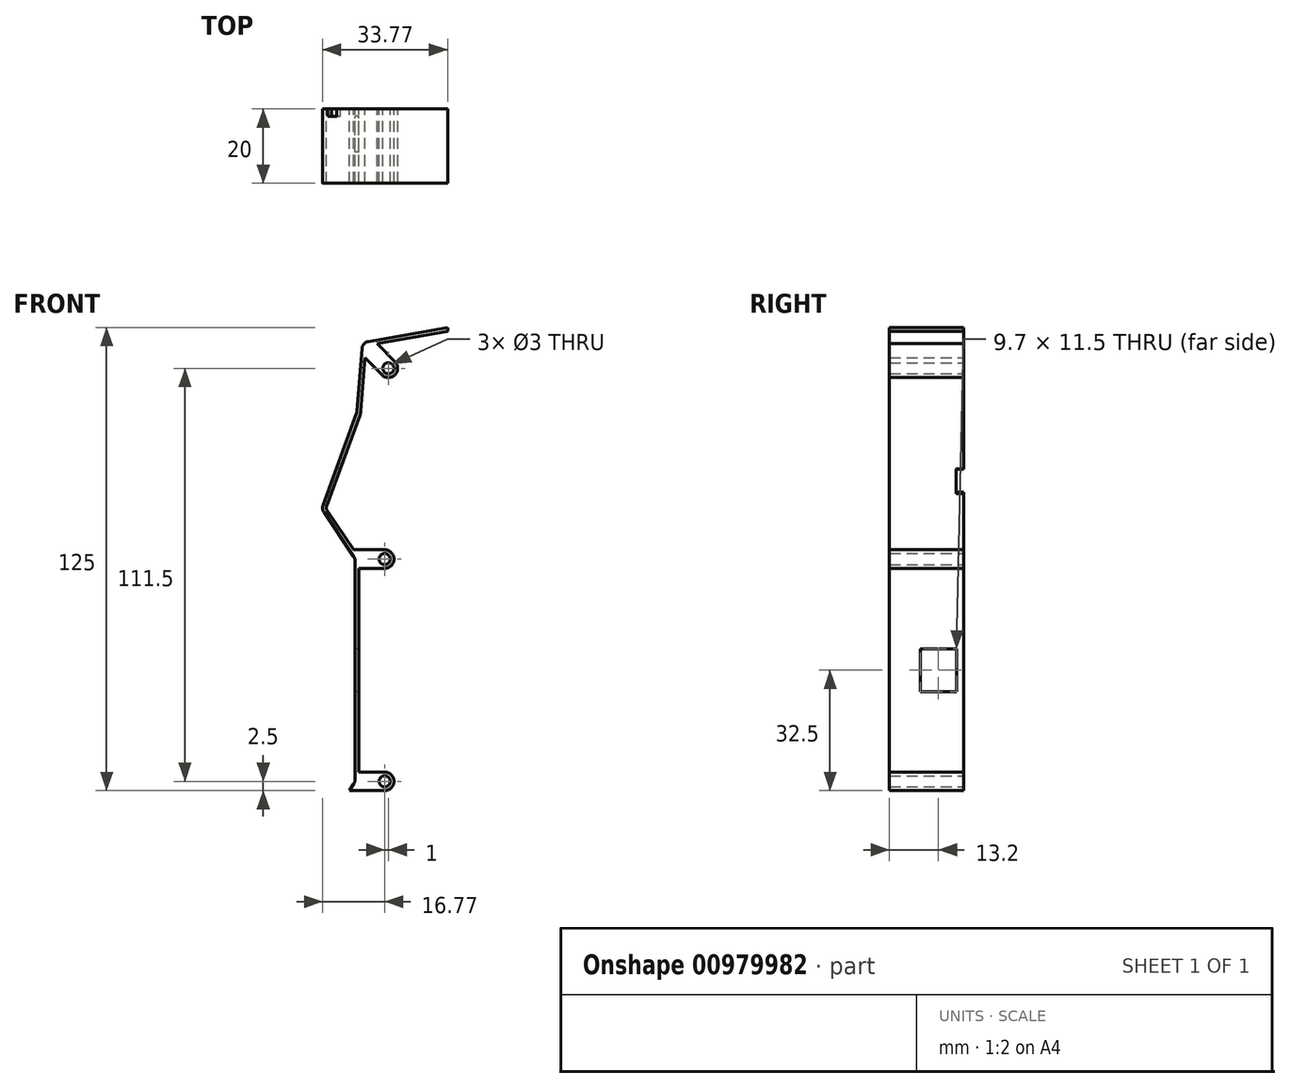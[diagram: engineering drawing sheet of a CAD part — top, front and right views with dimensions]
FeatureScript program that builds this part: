
annotation { "Feature Type Name" : "Feature", "Feature Type Description" : "" }
export const myFeature = defineFeature(function(context is Context, id is Id, definition is map)
    precondition{}
    {
        {
            var Q0;
            Q0=qCreatedBy(makeId("Front.planeOp"),FACE);
            var sketch = newSketch(context, id + "F0", { "sketchPlane" : qUnion([Q0])});
            skLineSegment(sketch, "E0", {"start": v(13, -77) * mm, "end": v(6, -77) * mm});
            skArc(sketch, "E1", {"start": v(33.65, -43.96) * mm, "mid": v(33.76, -43.03) * mm, "end": v(33.43, -42.16) * mm});
            skArc(sketch, "E2", {"start": v(33.43, 42.16) * mm, "mid": v(33.76, 43.03) * mm, "end": v(33.65, 43.96) * mm});
            skArc(sketch, "E3", {"start": v(-33.65, 43.96) * mm, "mid": v(-33.76, 43.03) * mm, "end": v(-33.43, 42.16) * mm});
            skArc(sketch, "E4", {"start": v(-33.43, -42.16) * mm, "mid": v(-33.76, -43.03) * mm, "end": v(-33.65, -43.96) * mm});
            skCircle(sketch, "E5", {"center": v(16, 81) * mm, "radius": 1.5 * mm});
            skCircle(sketch, "E6", {"center": v(0, 76) * mm, "radius": 1.5 * mm});
            skCircle(sketch, "E7", {"center": v(26.67, 45.42) * mm, "radius": 1.5 * mm});
            skCircle(sketch, "E8", {"center": v(22.4, 57.17) * mm, "radius": 1.5 * mm});
            skCircle(sketch, "E9", {"center": v(17.28, 42) * mm, "radius": 1.5 * mm});
            skCircle(sketch, "E10", {"center": v(13, 53.75) * mm, "radius": 1.5 * mm});
            skCircle(sketch, "E11", {"center": v(17, 29.5) * mm, "radius": 1.5 * mm});
            skCircle(sketch, "E12", {"center": v(15.25, 15.25) * mm, "radius": 1.5 * mm});
            skCircle(sketch, "E13", {"center": v(-15.25, 15.25) * mm, "radius": 1.5 * mm});
            skCircle(sketch, "E14", {"center": v(-17, 29.5) * mm, "radius": 1.5 * mm});
            skCircle(sketch, "E15", {"center": v(-13, 53.75) * mm, "radius": 1.5 * mm});
            skCircle(sketch, "E16", {"center": v(-17.28, 42) * mm, "radius": 1.5 * mm});
            skCircle(sketch, "E17", {"center": v(-22.4, 57.17) * mm, "radius": 1.5 * mm});
            skCircle(sketch, "E18", {"center": v(-26.67, 45.42) * mm, "radius": 1.5 * mm});
            skCircle(sketch, "E19", {"center": v(-16, 81) * mm, "radius": 1.5 * mm});
            skCircle(sketch, "E20", {"center": v(-16, -81) * mm, "radius": 1.5 * mm});
            skCircle(sketch, "E21", {"center": v(-26.67, -45.42) * mm, "radius": 1.5 * mm});
            skCircle(sketch, "E22", {"center": v(-22.4, -57.17) * mm, "radius": 1.5 * mm});
            skCircle(sketch, "E23", {"center": v(-17.28, -42) * mm, "radius": 1.5 * mm});
            skCircle(sketch, "E24", {"center": v(-13, -53.75) * mm, "radius": 1.5 * mm});
            skCircle(sketch, "E25", {"center": v(-17, -29.5) * mm, "radius": 1.5 * mm});
            skCircle(sketch, "E26", {"center": v(-15.25, -15.25) * mm, "radius": 1.5 * mm});
            skCircle(sketch, "E27", {"center": v(15.25, -15.25) * mm, "radius": 1.5 * mm});
            skCircle(sketch, "E28", {"center": v(17, -29.5) * mm, "radius": 1.5 * mm});
            skCircle(sketch, "E29", {"center": v(13, -53.75) * mm, "radius": 1.5 * mm});
            skCircle(sketch, "E30", {"center": v(17.28, -42) * mm, "radius": 1.5 * mm});
            skCircle(sketch, "E31", {"center": v(22.4, -57.17) * mm, "radius": 1.5 * mm});
            skCircle(sketch, "E32", {"center": v(26.67, -45.42) * mm, "radius": 1.5 * mm});
            skCircle(sketch, "E33", {"center": v(0, -76) * mm, "radius": 1.5 * mm});
            skCircle(sketch, "E34", {"center": v(16, -81) * mm, "radius": 1.5 * mm});
            skLineSegment(sketch, "E35", {"start": v(25.34, 30.16) * mm, "end": v(33.43, 42.16) * mm});
            skLineSegment(sketch, "E36", {"start": v(33.65, 43.96) * mm, "end": v(24.57, 68.9) * mm});
            skArc(sketch, "E37", {"start": v(24.46, 69.43) * mm, "mid": v(24.5, 69.16) * mm, "end": v(24.57, 68.9) * mm});
            skLineSegment(sketch, "E38", {"start": v(24.46, 69.43) * mm, "end": v(23.12, 86.4) * mm});
            skArc(sketch, "E39", {"start": v(23.12, 86.4) * mm, "mid": v(22.6, 87.59) * mm, "end": v(21.47, 88.21) * mm});
            skLineSegment(sketch, "E40", {"start": v(21.47, 88.21) * mm, "end": v(0, 92) * mm});
            skLineSegment(sketch, "E41", {"start": v(0, 92) * mm, "end": v(-21.47, 88.21) * mm});
            skArc(sketch, "E42", {"start": v(-21.47, 88.21) * mm, "mid": v(-22.6, 87.59) * mm, "end": v(-23.12, 86.4) * mm});
            skLineSegment(sketch, "E43", {"start": v(-23.12, 86.4) * mm, "end": v(-24.46, 69.43) * mm});
            skArc(sketch, "E44", {"start": v(-24.57, 68.9) * mm, "mid": v(-24.5, 69.16) * mm, "end": v(-24.46, 69.43) * mm});
            skLineSegment(sketch, "E45", {"start": v(-24.57, 68.9) * mm, "end": v(-33.65, 43.96) * mm});
            skLineSegment(sketch, "E46", {"start": v(-33.43, 42.16) * mm, "end": v(-25.34, 30.16) * mm});
            skArc(sketch, "E47", {"start": v(-25, 29.05) * mm, "mid": v(-25.09, 29.63) * mm, "end": v(-25.34, 30.16) * mm});
            skLineSegment(sketch, "E48", {"start": v(-25, 29.05) * mm, "end": v(-25, -29.05) * mm});
            skArc(sketch, "E49", {"start": v(-25.34, -30.16) * mm, "mid": v(-25.09, -29.63) * mm, "end": v(-25, -29.05) * mm});
            skLineSegment(sketch, "E50", {"start": v(-25.34, -30.16) * mm, "end": v(-33.43, -42.16) * mm});
            skLineSegment(sketch, "E51", {"start": v(-33.65, -43.96) * mm, "end": v(-24.57, -68.9) * mm});
            skArc(sketch, "E52", {"start": v(-24.46, -69.43) * mm, "mid": v(-24.5, -69.16) * mm, "end": v(-24.57, -68.9) * mm});
            skLineSegment(sketch, "E53", {"start": v(-24.46, -69.43) * mm, "end": v(-23.12, -86.4) * mm});
            skArc(sketch, "E54", {"start": v(-23.12, -86.4) * mm, "mid": v(-22.6, -87.59) * mm, "end": v(-21.47, -88.21) * mm});
            skLineSegment(sketch, "E55", {"start": v(-21.47, -88.21) * mm, "end": v(0, -92) * mm});
            skLineSegment(sketch, "E56", {"start": v(0, -92) * mm, "end": v(21.47, -88.21) * mm});
            skArc(sketch, "E57", {"start": v(21.47, -88.21) * mm, "mid": v(22.6, -87.59) * mm, "end": v(23.12, -86.4) * mm});
            skLineSegment(sketch, "E58", {"start": v(23.12, -86.4) * mm, "end": v(24.46, -69.43) * mm});
            skArc(sketch, "E59", {"start": v(24.57, -68.9) * mm, "mid": v(24.5, -69.16) * mm, "end": v(24.46, -69.43) * mm});
            skLineSegment(sketch, "E60", {"start": v(24.57, -68.9) * mm, "end": v(33.65, -43.96) * mm});
            skLineSegment(sketch, "E61", {"start": v(33.43, -42.16) * mm, "end": v(25.34, -30.16) * mm});
            skArc(sketch, "E62", {"start": v(25, -29.05) * mm, "mid": v(25.09, -29.63) * mm, "end": v(25.34, -30.16) * mm});
            skLineSegment(sketch, "E63", {"start": v(25, -29.05) * mm, "end": v(25, 29.05) * mm});
            skArc(sketch, "E64", {"start": v(25.34, 30.16) * mm, "mid": v(25.09, 29.63) * mm, "end": v(25, 29.05) * mm});
            skArc(sketch, "E65", {"start": v(14.5, -75) * mm, "mid": v(13.75, -74.25) * mm, "end": v(13, -75) * mm});
            skLineSegment(sketch, "E66", {"start": v(14.5, -75) * mm, "end": v(14.5, -77) * mm});
            skArc(sketch, "E67", {"start": v(13, -77) * mm, "mid": v(13.75, -77.75) * mm, "end": v(14.5, -77) * mm});
            skArc(sketch, "E68", {"start": v(4.5, -77) * mm, "mid": v(5.25, -77.75) * mm, "end": v(6, -77) * mm});
            skLineSegment(sketch, "E69", {"start": v(4.5, -77) * mm, "end": v(4.5, -75) * mm});
            skArc(sketch, "E70", {"start": v(6, -75) * mm, "mid": v(5.25, -74.25) * mm, "end": v(4.5, -75) * mm});
            skLineSegment(sketch, "E71", {"start": v(6, -75) * mm, "end": v(13, -75) * mm});
            skArc(sketch, "E72", {"start": v(-4.5, -75) * mm, "mid": v(-5.25, -74.25) * mm, "end": v(-6, -75) * mm});
            skLineSegment(sketch, "E73", {"start": v(-4.5, -75) * mm, "end": v(-4.5, -77) * mm});
            skArc(sketch, "E74", {"start": v(-6, -77) * mm, "mid": v(-5.25, -77.75) * mm, "end": v(-4.5, -77) * mm});
            skLineSegment(sketch, "E75", {"start": v(-6, -77) * mm, "end": v(-13, -77) * mm});
            skArc(sketch, "E76", {"start": v(-14.5, -77) * mm, "mid": v(-13.75, -77.75) * mm, "end": v(-13, -77) * mm});
            skLineSegment(sketch, "E77", {"start": v(-14.5, -77) * mm, "end": v(-14.5, -75) * mm});
            skArc(sketch, "E78", {"start": v(-13, -75) * mm, "mid": v(-13.75, -74.25) * mm, "end": v(-14.5, -75) * mm});
            skLineSegment(sketch, "E79", {"start": v(-13, -75) * mm, "end": v(-6, -75) * mm});
            skArc(sketch, "E80", {"start": v(-14.5, 75) * mm, "mid": v(-13.75, 74.25) * mm, "end": v(-13, 75) * mm});
            skLineSegment(sketch, "E81", {"start": v(-14.5, 75) * mm, "end": v(-14.5, 77) * mm});
            skArc(sketch, "E82", {"start": v(-13, 77) * mm, "mid": v(-13.75, 77.75) * mm, "end": v(-14.5, 77) * mm});
            skLineSegment(sketch, "E83", {"start": v(-13, 77) * mm, "end": v(-6, 77) * mm});
            skArc(sketch, "E84", {"start": v(-4.5, 77) * mm, "mid": v(-5.25, 77.75) * mm, "end": v(-6, 77) * mm});
            skLineSegment(sketch, "E85", {"start": v(-4.5, 77) * mm, "end": v(-4.5, 75) * mm});
            skArc(sketch, "E86", {"start": v(-6, 75) * mm, "mid": v(-5.25, 74.25) * mm, "end": v(-4.5, 75) * mm});
            skLineSegment(sketch, "E87", {"start": v(-6, 75) * mm, "end": v(-13, 75) * mm});
            skArc(sketch, "E88", {"start": v(6, 77) * mm, "mid": v(5.25, 77.75) * mm, "end": v(4.5, 77) * mm});
            skLineSegment(sketch, "E89", {"start": v(6, 77) * mm, "end": v(13, 77) * mm});
            skArc(sketch, "E90", {"start": v(14.5, 77) * mm, "mid": v(13.75, 77.75) * mm, "end": v(13, 77) * mm});
            skLineSegment(sketch, "E91", {"start": v(14.5, 77) * mm, "end": v(14.5, 75) * mm});
            skArc(sketch, "E92", {"start": v(13, 75) * mm, "mid": v(13.75, 74.25) * mm, "end": v(14.5, 75) * mm});
            skLineSegment(sketch, "E93", {"start": v(13, 75) * mm, "end": v(6, 75) * mm});
            skArc(sketch, "E94", {"start": v(4.5, 75) * mm, "mid": v(5.25, 74.25) * mm, "end": v(6, 75) * mm});
            skLineSegment(sketch, "E95", {"start": v(4.5, 75) * mm, "end": v(4.5, 77) * mm});
            skLineSegment(sketch, "E96", {"start": v(18, 7) * mm, "end": v(18, -7) * mm});
            skArc(sketch, "E97", {"start": v(20, 7) * mm, "mid": v(19, 8) * mm, "end": v(18, 7) * mm});
            skLineSegment(sketch, "E98", {"start": v(20, -7) * mm, "end": v(20, 7) * mm});
            skArc(sketch, "E99", {"start": v(18, -7) * mm, "mid": v(19, -8) * mm, "end": v(20, -7) * mm});
            skLineSegment(sketch, "E100", {"start": v(11, -37.25) * mm, "end": v(11, -20.25) * mm});
            skArc(sketch, "E101", {"start": v(8, -37.25) * mm, "mid": v(9.5, -38.75) * mm, "end": v(11, -37.25) * mm});
            skLineSegment(sketch, "E102", {"start": v(8, -20.25) * mm, "end": v(8, -37.25) * mm});
            skArc(sketch, "E103", {"start": v(11, -20.25) * mm, "mid": v(9.5, -18.75) * mm, "end": v(8, -20.25) * mm});
            skLineSegment(sketch, "E104", {"start": v(-9.2, -70.25) * mm, "end": v(-9.2, -58.25) * mm});
            skArc(sketch, "E105", {"start": v(-11.2, -70.25) * mm, "mid": v(-10.2, -71.25) * mm, "end": v(-9.2, -70.25) * mm});
            skLineSegment(sketch, "E106", {"start": v(-11.2, -58.25) * mm, "end": v(-11.2, -70.25) * mm});
            skArc(sketch, "E107", {"start": v(-9.2, -58.25) * mm, "mid": v(-10.2, -57.25) * mm, "end": v(-11.2, -58.25) * mm});
            skLineSegment(sketch, "E108", {"start": v(5, -69.25) * mm, "end": v(5, -58.25) * mm});
            skArc(sketch, "E109", {"start": v(3, -71.25) * mm, "mid": v(4.41, -70.66) * mm, "end": v(5, -69.25) * mm});
            skLineSegment(sketch, "E110", {"start": v(-3, -71.25) * mm, "end": v(3, -71.25) * mm});
            skArc(sketch, "E111", {"start": v(-5, -69.25) * mm, "mid": v(-4.41, -70.66) * mm, "end": v(-3, -71.25) * mm});
            skLineSegment(sketch, "E112", {"start": v(-5, -58.25) * mm, "end": v(-5, -69.25) * mm});
            skArc(sketch, "E113", {"start": v(-3, -56.25) * mm, "mid": v(-4.41, -56.84) * mm, "end": v(-5, -58.25) * mm});
            skLineSegment(sketch, "E114", {"start": v(3, -56.25) * mm, "end": v(-3, -56.25) * mm});
            skArc(sketch, "E115", {"start": v(5, -58.25) * mm, "mid": v(4.41, -56.84) * mm, "end": v(3, -56.25) * mm});
            skLineSegment(sketch, "E116", {"start": v(-11, 37.25) * mm, "end": v(-11, 20.25) * mm});
            skArc(sketch, "E117", {"start": v(-8, 37.25) * mm, "mid": v(-9.5, 38.75) * mm, "end": v(-11, 37.25) * mm});
            skLineSegment(sketch, "E118", {"start": v(-8, 20.25) * mm, "end": v(-8, 37.25) * mm});
            skArc(sketch, "E119", {"start": v(-11, 20.25) * mm, "mid": v(-9.5, 18.75) * mm, "end": v(-8, 20.25) * mm});
            skLineSegment(sketch, "E120", {"start": v(9.2, 70.25) * mm, "end": v(9.2, 58.25) * mm});
            skArc(sketch, "E121", {"start": v(11.2, 70.25) * mm, "mid": v(10.2, 71.25) * mm, "end": v(9.2, 70.25) * mm});
            skLineSegment(sketch, "E122", {"start": v(11.2, 58.25) * mm, "end": v(11.2, 70.25) * mm});
            skArc(sketch, "E123", {"start": v(9.2, 58.25) * mm, "mid": v(10.2, 57.25) * mm, "end": v(11.2, 58.25) * mm});
            skLineSegment(sketch, "E124", {"start": v(-5, 69.25) * mm, "end": v(-5, 58.25) * mm});
            skArc(sketch, "E125", {"start": v(-3, 71.25) * mm, "mid": v(-4.41, 70.66) * mm, "end": v(-5, 69.25) * mm});
            skLineSegment(sketch, "E126", {"start": v(3, 71.25) * mm, "end": v(-3, 71.25) * mm});
            skArc(sketch, "E127", {"start": v(5, 69.25) * mm, "mid": v(4.41, 70.66) * mm, "end": v(3, 71.25) * mm});
            skLineSegment(sketch, "E128", {"start": v(5, 58.25) * mm, "end": v(5, 69.25) * mm});
            skArc(sketch, "E129", {"start": v(3, 56.25) * mm, "mid": v(4.41, 56.84) * mm, "end": v(5, 58.25) * mm});
            skLineSegment(sketch, "E130", {"start": v(-3, 56.25) * mm, "end": v(3, 56.25) * mm});
            skArc(sketch, "E131", {"start": v(-5, 58.25) * mm, "mid": v(-4.41, 56.84) * mm, "end": v(-3, 56.25) * mm});
            skLineSegment(sketch, "E132", {"start": v(-3, 20.25) * mm, "end": v(3, 20.25) * mm});
            skArc(sketch, "E133", {"start": v(-5, 22.25) * mm, "mid": v(-4.41, 20.84) * mm, "end": v(-3, 20.25) * mm});
            skLineSegment(sketch, "E134", {"start": v(-5, 36.25) * mm, "end": v(-5, 22.25) * mm});
            skArc(sketch, "E135", {"start": v(-3, 38.25) * mm, "mid": v(-4.41, 37.66) * mm, "end": v(-5, 36.25) * mm});
            skLineSegment(sketch, "E136", {"start": v(3, 38.25) * mm, "end": v(-3, 38.25) * mm});
            skArc(sketch, "E137", {"start": v(5, 36.25) * mm, "mid": v(4.41, 37.66) * mm, "end": v(3, 38.25) * mm});
            skLineSegment(sketch, "E138", {"start": v(5, 22.25) * mm, "end": v(5, 36.25) * mm});
            skArc(sketch, "E139", {"start": v(3, 20.25) * mm, "mid": v(4.41, 20.84) * mm, "end": v(5, 22.25) * mm});
            skLineSegment(sketch, "E140", {"start": v(13.25, 8.75) * mm, "end": v(-13.25, 8.75) * mm});
            skArc(sketch, "E141", {"start": v(14.75, 7.25) * mm, "mid": v(14.31, 8.31) * mm, "end": v(13.25, 8.75) * mm});
            skLineSegment(sketch, "E142", {"start": v(14.75, -7.25) * mm, "end": v(14.75, 7.25) * mm});
            skArc(sketch, "E143", {"start": v(13.25, -8.75) * mm, "mid": v(14.31, -8.31) * mm, "end": v(14.75, -7.25) * mm});
            skLineSegment(sketch, "E144", {"start": v(-13.25, -8.75) * mm, "end": v(13.25, -8.75) * mm});
            skArc(sketch, "E145", {"start": v(-14.75, -7.25) * mm, "mid": v(-14.31, -8.31) * mm, "end": v(-13.25, -8.75) * mm});
            skLineSegment(sketch, "E146", {"start": v(-14.75, 7.25) * mm, "end": v(-14.75, -7.25) * mm});
            skArc(sketch, "E147", {"start": v(-13.25, 8.75) * mm, "mid": v(-14.31, 8.31) * mm, "end": v(-14.75, 7.25) * mm});
            skLineSegment(sketch, "E148", {"start": v(8, 37.25) * mm, "end": v(8, 20.25) * mm});
            skArc(sketch, "E149", {"start": v(11, 37.25) * mm, "mid": v(9.5, 38.75) * mm, "end": v(8, 37.25) * mm});
            skLineSegment(sketch, "E150", {"start": v(11, 20.25) * mm, "end": v(11, 37.25) * mm});
            skArc(sketch, "E151", {"start": v(8, 20.25) * mm, "mid": v(9.5, 18.75) * mm, "end": v(11, 20.25) * mm});
            skLineSegment(sketch, "E152", {"start": v(-11.2, 70.25) * mm, "end": v(-11.2, 58.25) * mm});
            skArc(sketch, "E153", {"start": v(-9.2, 70.25) * mm, "mid": v(-10.2, 71.25) * mm, "end": v(-11.2, 70.25) * mm});
            skLineSegment(sketch, "E154", {"start": v(-9.2, 58.25) * mm, "end": v(-9.2, 70.25) * mm});
            skArc(sketch, "E155", {"start": v(-11.2, 58.25) * mm, "mid": v(-10.2, 57.25) * mm, "end": v(-9.2, 58.25) * mm});
            skLineSegment(sketch, "E156", {"start": v(-3, -38.25) * mm, "end": v(3, -38.25) * mm});
            skArc(sketch, "E157", {"start": v(-5, -36.25) * mm, "mid": v(-4.41, -37.66) * mm, "end": v(-3, -38.25) * mm});
            skLineSegment(sketch, "E158", {"start": v(-5, -22.25) * mm, "end": v(-5, -36.25) * mm});
            skArc(sketch, "E159", {"start": v(-3, -20.25) * mm, "mid": v(-4.41, -20.84) * mm, "end": v(-5, -22.25) * mm});
            skLineSegment(sketch, "E160", {"start": v(3, -20.25) * mm, "end": v(-3, -20.25) * mm});
            skArc(sketch, "E161", {"start": v(5, -22.25) * mm, "mid": v(4.41, -20.84) * mm, "end": v(3, -20.25) * mm});
            skLineSegment(sketch, "E162", {"start": v(5, -36.25) * mm, "end": v(5, -22.25) * mm});
            skArc(sketch, "E163", {"start": v(3, -38.25) * mm, "mid": v(4.41, -37.66) * mm, "end": v(5, -36.25) * mm});
            skLineSegment(sketch, "E164", {"start": v(-8, -37.25) * mm, "end": v(-8, -20.25) * mm});
            skArc(sketch, "E165", {"start": v(-11, -37.25) * mm, "mid": v(-9.5, -38.75) * mm, "end": v(-8, -37.25) * mm});
            skLineSegment(sketch, "E166", {"start": v(-11, -20.25) * mm, "end": v(-11, -37.25) * mm});
            skArc(sketch, "E167", {"start": v(-8, -20.25) * mm, "mid": v(-9.5, -18.75) * mm, "end": v(-11, -20.25) * mm});
            skLineSegment(sketch, "E168", {"start": v(11.2, -70.25) * mm, "end": v(11.2, -58.25) * mm});
            skArc(sketch, "E169", {"start": v(9.2, -70.25) * mm, "mid": v(10.2, -71.25) * mm, "end": v(11.2, -70.25) * mm});
            skLineSegment(sketch, "E170", {"start": v(9.2, -58.25) * mm, "end": v(9.2, -70.25) * mm});
            skArc(sketch, "E171", {"start": v(11.2, -58.25) * mm, "mid": v(10.2, -57.25) * mm, "end": v(9.2, -58.25) * mm});
            skLineSegment(sketch, "E172", {"start": v(-20, 7) * mm, "end": v(-20, -7) * mm});
            skArc(sketch, "E173", {"start": v(-18, 7) * mm, "mid": v(-19, 8) * mm, "end": v(-20, 7) * mm});
            skLineSegment(sketch, "E174", {"start": v(-18, -7) * mm, "end": v(-18, 7) * mm});
            skArc(sketch, "E175", {"start": v(-20, -7) * mm, "mid": v(-19, -8) * mm, "end": v(-18, -7) * mm});
            skSolve(sketch);
        }
        {
            var Q0;
            Q0=qCreatedBy(makeId("Front.planeOp"),FACE);
            var sketch = newSketch(context, id + "F1", { "sketchPlane" : qUnion([Q0])});
            skArc(sketch, "E176", {"start": v(-17.79, 79.25) * mm, "mid": v(-14.25, 79.21) * mm, "end": v(-14.21, 82.75) * mm});
            skArc(sketch, "E177", {"start": v(-17, 27) * mm, "mid": v(-14.5, 29.5) * mm, "end": v(-17, 32) * mm});
            skLineSegment(sketch, "E178.0.18", {"start": v(0, 92) * mm, "end": v(-21.47, 88.21) * mm});
            skArc(sketch, "E178.0.19", {"start": v(-21.47, 88.21) * mm, "mid": v(-22.6, 87.59) * mm, "end": v(-23.12, 86.4) * mm});
            skLineSegment(sketch, "E178.0.20", {"start": v(-23.12, 86.4) * mm, "end": v(-24.46, 69.43) * mm});
            skArc(sketch, "E178.0.21", {"start": v(-24.46, 69.43) * mm, "mid": v(-24.5, 69.16) * mm, "end": v(-24.57, 68.9) * mm});
            skLineSegment(sketch, "E178.0.22", {"start": v(-24.57, 68.9) * mm, "end": v(-33.65, 43.96) * mm});
            skArc(sketch, "E178.0.23", {"start": v(-33.65, 43.96) * mm, "mid": v(-33.76, 43.03) * mm, "end": v(-33.43, 42.16) * mm});
            skLineSegment(sketch, "E178.0.24", {"start": v(-33.43, 42.16) * mm, "end": v(-25.34, 30.16) * mm});
            skArc(sketch, "E178.0.25", {"start": v(-25.34, 30.16) * mm, "mid": v(-25.09, 29.63) * mm, "end": v(-25, 29.05) * mm});
            skLineSegment(sketch, "E178.0.26", {"start": v(-25, 29.05) * mm, "end": v(-25, -0.5) * mm});
            skLineSegment(sketch, "E179", {"start": v(0, 90.98) * mm, "end": v(-14.59, 88.41) * mm});
            skArc(sketch, "E180", {"start": v(-21.3, 87.23) * mm, "mid": v(-21.87, 86.92) * mm, "end": v(-22.12, 86.32) * mm});
            skLineSegment(sketch, "E181", {"start": v(-1.94, 91.66) * mm, "end": v(-1.77, 90.67) * mm, "construction": true});
            skArc(sketch, "E182", {"start": v(-23.63, 68.56) * mm, "mid": v(-23.52, 68.95) * mm, "end": v(-23.46, 69.35) * mm});
            skLineSegment(sketch, "E183", {"start": v(-23.63, 68.56) * mm, "end": v(-32.71, 43.62) * mm});
            skArc(sketch, "E184", {"start": v(-32.71, 43.62) * mm, "mid": v(-32.76, 43.15) * mm, "end": v(-32.6, 42.71) * mm});
            skArc(sketch, "E185", {"start": v(-24, 29.05) * mm, "mid": v(-24.13, 29.92) * mm, "end": v(-24.51, 30.72) * mm});
            skLineSegment(sketch, "E186", {"start": v(-32.6, 42.71) * mm, "end": v(-25.37, 32) * mm});
            skLineSegment(sketch, "E187", {"start": v(-24, 27) * mm, "end": v(-24, -0.5) * mm});
            skLineSegment(sketch, "E188.bottom", {"start": v(-17, 32) * mm, "end": v(-25, 32) * mm});
            skLineSegment(sketch, "E188.top", {"start": v(-17, 27) * mm, "end": v(-24, 27) * mm});
            skLineSegment(sketch, "E189.trimOffspring", {"start": v(-25, 29.05) * mm, "end": v(-25, 27) * mm});
            skLineSegment(sketch, "E190.trimOffspring", {"start": v(-22.57, 80.65) * mm, "end": v(-23.46, 69.35) * mm});
            skLineSegment(sketch, "E191.trimOffspring", {"start": v(-17.59, 87.88) * mm, "end": v(-19, 87.64) * mm});
            skPoint(sketch, "E192.orphan", {"position": v(-33.43, -42.16) * mm});
            skLineSegment(sketch, "E193", {"start": v(0, 90.98) * mm, "end": v(0, 92) * mm});
            skLineSegment(sketch, "E194", {"start": v(-22.32, 83.88) * mm, "end": v(-17.79, 79.25) * mm});
            skLineSegment(sketch, "E195", {"start": v(-14.21, 82.75) * mm, "end": v(-19, 87.64) * mm});
            skLineSegment(sketch, "E196", {"start": v(-21.13, 86.24) * mm, "end": v(-16, 81) * mm, "construction": true});
            skLineSegment(sketch, "E197", {"start": v(-17.59, 87.88) * mm, "end": v(-14.59, 88.41) * mm});
            skPoint(sketch, "E198.orphan", {"position": v(-17.5, 87.92) * mm});
            skPoint(sketch, "E199.orphan", {"position": v(-17.5, 83.6) * mm});
            skPoint(sketch, "E200.orphan", {"position": v(-18.17, 79.75) * mm});
            skPoint(sketch, "E201.orphan", {"position": v(-18.6, 82.5) * mm});
            skLineSegment(sketch, "E202", {"start": v(-22.32, 83.88) * mm, "end": v(-22.57, 80.65) * mm});
            skPoint(sketch, "E203.orphan", {"position": v(-22.16, 82.5) * mm});
            skPoint(sketch, "E204.right.start.orphan", {"position": v(-14.75, 83.17) * mm});
            skCircle(sketch, "E205", {"center": v(-17, 29.5) * mm, "radius": 1.5 * mm});
            skCircle(sketch, "E206", {"center": v(-16, 81) * mm, "radius": 1.5 * mm});
            skLineSegment(sketch, "E207", {"start": v(-67.15, -0.5) * mm, "end": v(71.74, -0.5) * mm});
            skLineSegment(sketch, "E208.MirrorCS", {"start": v(-25, -30.05) * mm, "end": v(-25, -0.5) * mm});
            skLineSegment(sketch, "E209.MirrorCS", {"start": v(-24, -28) * mm, "end": v(-24, -0.5) * mm});
            skLineSegment(sketch, "E210.MirrorCS", {"start": v(-17, -28) * mm, "end": v(-24, -28) * mm});
            skArc(sketch, "E211.MirrorCS", {"start": v(-17, -28) * mm, "mid": v(-14.5, -30.5) * mm, "end": v(-17, -33) * mm});
            skLineSegment(sketch, "E212.MirrorCS", {"start": v(-17, -33) * mm, "end": v(-25, -33) * mm});
            skCircle(sketch, "E213.MirrorC", {"center": v(-17, -30.5) * mm, "radius": 1.5 * mm});
            skArc(sketch, "E214.MirrorCS", {"start": v(-25.34, -31.16) * mm, "mid": v(-25.09, -30.63) * mm, "end": v(-25, -30.05) * mm});
            skLineSegment(sketch, "E215.MirrorCS", {"start": v(-26.58, -33) * mm, "end": v(-25.34, -31.16) * mm});
            skLineSegment(sketch, "E216", {"start": v(-25, -33) * mm, "end": v(-26.58, -33) * mm});
            skPoint(sketch, "E217.orphan", {"position": v(-33.43, -43.16) * mm});
            skLineSegment(sketch, "E218", {"start": v(-22.12, 86.32) * mm, "end": v(-22.32, 83.88) * mm});
            skLineSegment(sketch, "E219", {"start": v(-25, 32) * mm, "end": v(-25.67, 32) * mm});
            skSolve(sketch);
        }
        {
            var Q0;
            Q0 = qSketchRegion(id + "F1", true);
            extrude(context, id + "F2", {"entities" : qUnion([Q0]), "depth" : 20 * mm, "offsetDistance" : 25 * mm});
        }
        {
            var Q0;
            Q0=makeQuery(id+"F2.opExtrude","SWEPT_FACE",FACE,{"disambiguationData":[OSD([sQuery(id+"F1.wireOp",EDGE,"E178.0.22")])]});
            var sketch = newSketch(context, id + "F3", { "sketchPlane" : qUnion([Q0])});
            skLineSegment(sketch, "E220.bottom", {"start": v(2, 40.62) * mm, "end": v(0, 40.62) * mm});
            skLineSegment(sketch, "E220.top", {"start": v(2, 33.62) * mm, "end": v(0, 33.62) * mm});
            skLineSegment(sketch, "E220.left", {"start": v(2, 40.62) * mm, "end": v(2, 33.62) * mm});
            skLineSegment(sketch, "E220.right", {"start": v(0, 40.62) * mm, "end": v(0, 33.62) * mm});
            skSolve(sketch);
        }
        {
            var Q0;
            Q0 = qSketchRegion(id + "F3", true);
            extrude(context, id + "F4", {"entities" : qUnion([Q0]), "operationType" : NewBodyOperationType.REMOVE, "oppositeDirection" : true, "depth" : 25 * mm, "offsetDistance" : 25 * mm});
        }
        {
            var Q0;
            Q0=makeQuery(id+"F2.opExtrude","SWEPT_FACE",FACE,{"disambiguationData":[OSD([sQuery(id+"F1.wireOp",EDGE,"E178.0.26"),sQuery(id+"F1.wireOp",EDGE,"E189.trimOffspring"),sQuery(id+"F1.wireOp",EDGE,"E208.MirrorCS")])]});
            var sketch = newSketch(context, id + "F5", { "sketchPlane" : qUnion([Q0])});
            skLineSegment(sketch, "E221.bottom", {"start": v(11.65, 5.25) * mm, "end": v(1.95, 5.25) * mm});
            skLineSegment(sketch, "E221.top", {"start": v(11.65, -6.25) * mm, "end": v(1.95, -6.25) * mm});
            skLineSegment(sketch, "E221.left", {"start": v(11.65, 5.25) * mm, "end": v(11.65, -6.25) * mm});
            skLineSegment(sketch, "E221.right", {"start": v(1.95, 5.25) * mm, "end": v(1.95, -6.25) * mm});
            skLineSegment(sketch, "E222", {"start": v(11.65, -6.25) * mm, "end": v(6.8, -0.5) * mm, "construction": true});
            skLineSegment(sketch, "E223", {"start": v(1.95, 5.25) * mm, "end": v(6.8, -0.5) * mm, "construction": true});
            skLineSegment(sketch, "E224", {"start": v(11.65, 5.25) * mm, "end": v(11.65, 29.05) * mm});
            skLineSegment(sketch, "E225", {"start": v(11.65, -6.25) * mm, "end": v(11.65, -30.05) * mm});
            skSolve(sketch);
        }
        {
            var Q0;
            Q0 = qSketchRegion(id + "F5", true);
            extrude(context, id + "F6", {"entities" : qUnion([Q0]), "operationType" : NewBodyOperationType.REMOVE, "oppositeDirection" : true, "depth" : 25 * mm, "offsetDistance" : 25 * mm});
        }
    });
